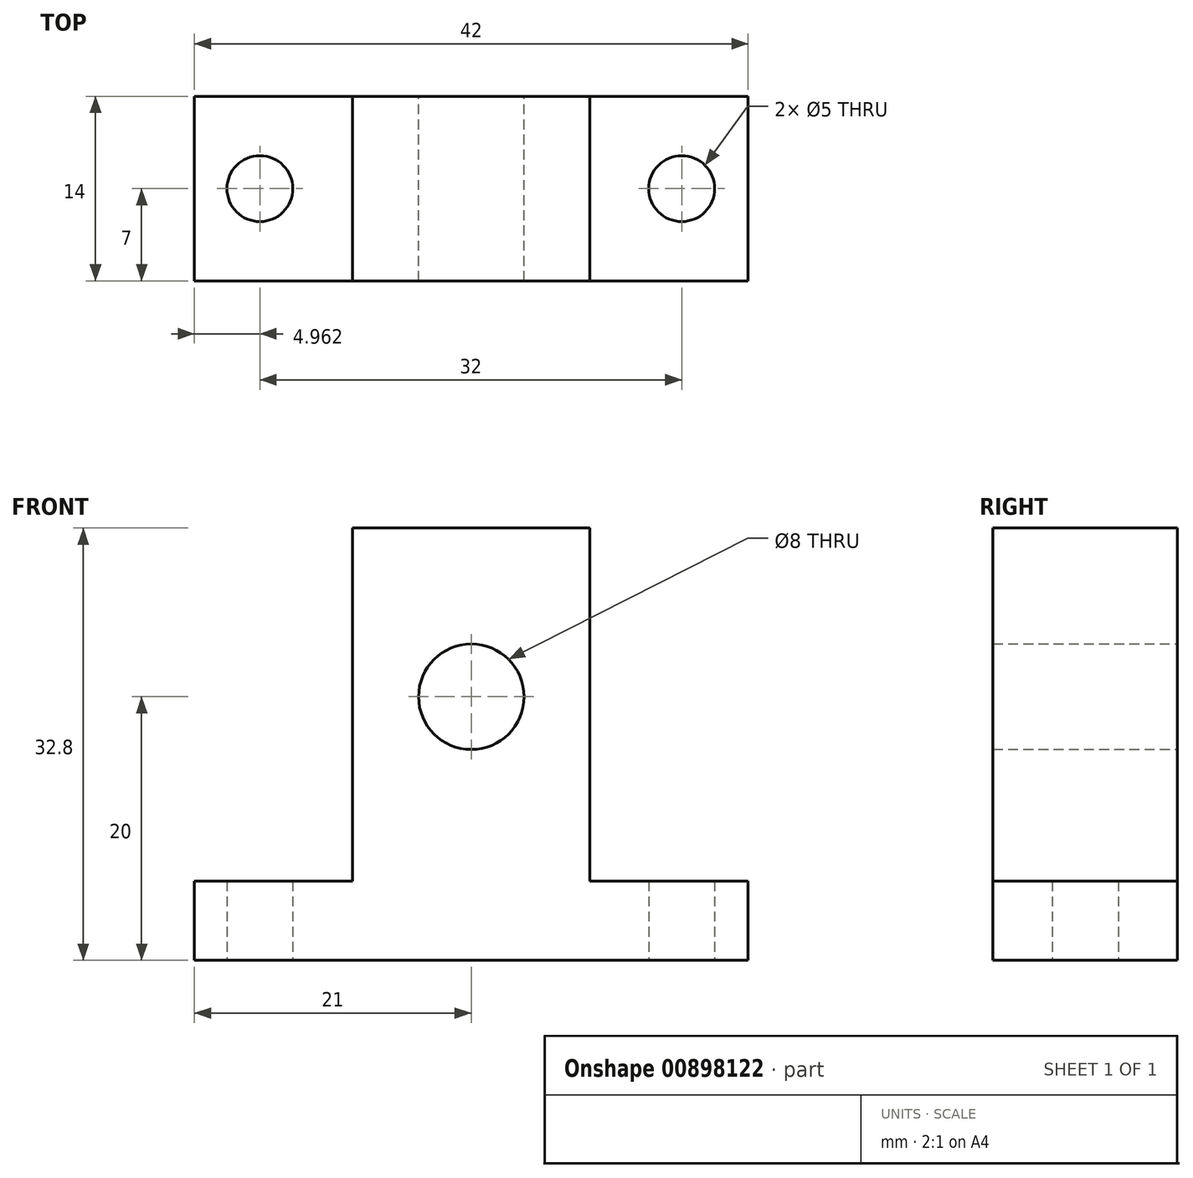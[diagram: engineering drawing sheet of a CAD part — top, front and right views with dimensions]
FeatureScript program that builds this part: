
annotation { "Feature Type Name" : "Feature", "Feature Type Description" : "" }
export const myFeature = defineFeature(function(context is Context, id is Id, definition is map)
    precondition{}
    {
        {
            var Q0;
            Q0=qCreatedBy(makeId("Front.planeOp"),FACE);
            var sketch = newSketch(context, id + "F0", { "sketchPlane" : qUnion([Q0])});
            skLineSegment(sketch, "E0", {"start": v(0, 0) * mm, "end": v(9, 0) * mm});
            skLineSegment(sketch, "E1", {"start": v(9, 0) * mm, "end": v(9, 32.8) * mm});
            skLineSegment(sketch, "E2", {"start": v(9, 32.8) * mm, "end": v(0, 32.8) * mm});
            skLineSegment(sketch, "E3", {"start": v(0, 32.8) * mm, "end": v(-9, 32.8) * mm});
            skLineSegment(sketch, "E4", {"start": v(-9, 32.8) * mm, "end": v(-9, 0) * mm});
            skLineSegment(sketch, "E5", {"start": v(-9, 0) * mm, "end": v(0, 0) * mm});
            skLineSegment(sketch, "E6", {"start": v(-9, 0) * mm, "end": v(-21, 0) * mm});
            skLineSegment(sketch, "E7", {"start": v(-21, 0) * mm, "end": v(-21, 6) * mm});
            skLineSegment(sketch, "E8", {"start": v(-21, 6) * mm, "end": v(-9, 6) * mm});
            skLineSegment(sketch, "E9", {"start": v(-9, 6) * mm, "end": v(-9, 0) * mm});
            skLineSegment(sketch, "E10.MirrorCS", {"start": v(9, 0) * mm, "end": v(21, 0) * mm});
            skLineSegment(sketch, "E11.MirrorCS", {"start": v(21, 6) * mm, "end": v(9, 6) * mm});
            skLineSegment(sketch, "E12.MirrorCS", {"start": v(21, 0) * mm, "end": v(21, 6) * mm});
            skPoint(sketch, "E13", {"position": v(0, 20) * mm});
            skCircle(sketch, "E14", {"center": v(0, 20) * mm, "radius": 4 * mm});
            skSolve(sketch);
        }
        {
            var Q0;
            {var subQ0=sQuery(id+"F0.wireOp",EDGE,"E6");Q0=makeQuery(id+"F0.imprint","IMPRINT",FACE,{"disambiguationData":[TD([[makeQuery(id+"F0.imprint","IMPRINT",EDGE,{"derivedFrom":subQ0}),-1.0]])]});}
            var Q1;
            {var subQ2=sQuery(id+"F0.wireOp",EDGE,"E0");Q1=makeQuery(id+"F0.imprint","IMPRINT",FACE,{"disambiguationData":[TD([[makeQuery(id+"F0.imprint","IMPRINT",EDGE,{"derivedFrom":subQ2}),1.0]])]});}
            var Q2;
            {var subQ0=sQuery(id+"F0.wireOp",EDGE,"E10.MirrorCS");Q2=makeQuery(id+"F0.imprint","IMPRINT",FACE,{"disambiguationData":[TD([[makeQuery(id+"F0.imprint","IMPRINT",EDGE,{"derivedFrom":subQ0}),1.0]])]});}
            extrude(context, id + "F1", {"entities" : qUnion([Q0, Q1, Q2]), "depth" : 14 * mm, "offsetDistance" : 25 * mm});
        }
        {
            var Q0;
            Q0=qCreatedBy(makeId("Top.planeOp"),FACE);
            var sketch = newSketch(context, id + "F2", { "sketchPlane" : qUnion([Q0])});
            skLineSegment(sketch, "E15", {"start": v(-21.04, 0) * mm, "end": v(-21.04, -14) * mm});
            skLineSegment(sketch, "E16", {"start": v(-21.04, -14) * mm, "end": v(20.96, -14) * mm});
            skLineSegment(sketch, "E17", {"start": v(20.96, -14) * mm, "end": v(20.96, 0) * mm});
            skLineSegment(sketch, "E18", {"start": v(20.96, 0) * mm, "end": v(-21.04, 0) * mm});
            skPoint(sketch, "E19", {"position": v(-16.04, -7) * mm});
            skPoint(sketch, "E20", {"position": v(15.96, -7) * mm});
            skCircle(sketch, "E21", {"center": v(-16.04, -7) * mm, "radius": 2.75 * mm});
            skCircle(sketch, "E22", {"center": v(15.96, -7) * mm, "radius": 2.75 * mm});
            skSolve(sketch);
        }
        {
            var Q0;
            Q0=sQuery(id+"F2.wireOp",VERTEX,"E19");
            var Q1;
            Q1=sQuery(id+"F2.wireOp",VERTEX,"E20");
            var Q2;
            Q2=makeQuery(id+"F1.opExtrude","SWEPT_BODY",BODY,{"disambiguationData":[OSD([sQuery(id+"F0.wireOp",EDGE,"E0"),sQuery(id+"F0.wireOp",EDGE,"E1"),sQuery(id+"F0.wireOp",EDGE,"E2"),sQuery(id+"F0.wireOp",EDGE,"E3"),sQuery(id+"F0.wireOp",EDGE,"E4"),sQuery(id+"F0.wireOp",EDGE,"E5"),sQuery(id+"F0.wireOp",EDGE,"E6"),sQuery(id+"F0.wireOp",EDGE,"E7"),sQuery(id+"F0.wireOp",EDGE,"E8"),sQuery(id+"F0.wireOp",EDGE,"E10.MirrorCS"),sQuery(id+"F0.wireOp",EDGE,"E11.MirrorCS"),sQuery(id+"F0.wireOp",EDGE,"E12.MirrorCS"),sQuery(id+"F0.wireOp",EDGE,"E14")])]});
            hole(context, id + "F3", {"style" : HoleStyle.SIMPLE, "endStyle" : HoleEndStyle.BLIND, "oppositeDirection" : true, "holeDiameter" : 5 * mm, "majorDiameter" : 5 * mm, "holeDepth" : 6 * mm, "isTappedThrough" : true, "tappedDepth" : 12 * mm, "tapClearance" : 3, "locations" : qUnion([Q0, Q1]), "scope" : qUnion([Q2])});
        }
    });
